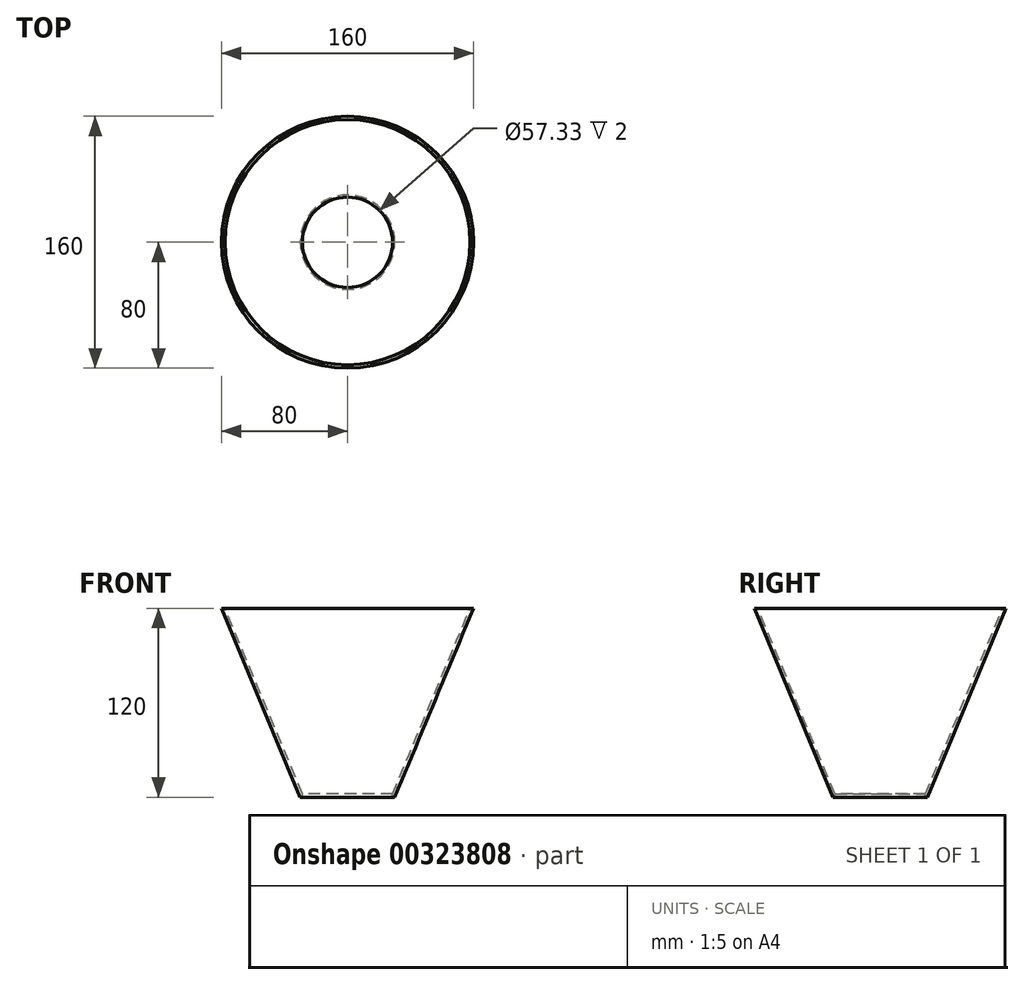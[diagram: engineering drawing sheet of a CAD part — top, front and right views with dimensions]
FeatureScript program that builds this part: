
annotation { "Feature Type Name" : "Feature", "Feature Type Description" : "" }
export const myFeature = defineFeature(function(context is Context, id is Id, definition is map)
    precondition{}
    {
        {
            var Q0;
            Q0=qCreatedBy(makeId("Front.planeOp"),FACE);
            var sketch = newSketch(context, id + "F0", { "sketchPlane" : qUnion([Q0])});
            skLineSegment(sketch, "E0", {"start": v(0, 0) * mm, "end": v(0, -120) * mm});
            skLineSegment(sketch, "E1", {"start": v(0, 0) * mm, "end": v(0, 240) * mm});
            skLineSegment(sketch, "E2", {"start": v(0, 240) * mm, "end": v(-180, 240) * mm});
            skLineSegment(sketch, "E3", {"start": v(0, -120) * mm, "end": v(-30, -120) * mm});
            skLineSegment(sketch, "E4", {"start": v(-180, 240) * mm, "end": v(-30, -120) * mm});
            skLineSegment(sketch, "E5", {"start": v(0, 0) * mm, "end": v(-80, 0) * mm});
            skSolve(sketch);
        }
        {
            var Q0;
            Q0=makeQuery(id+"F0.imprint","IMPRINT",FACE,{"disambiguationData":[TD([[makeQuery(id+"F0.imprint","IMPRINT",EDGE,{"derivedFrom":sQuery(id+"F0.wireOp",EDGE,"E0")}),-1.0]])]});
            var Q1;
            Q1=sQuery(id+"F0.wireOp",EDGE,"E0");
            revolve(context, id + "F1", {"entities" : qUnion([Q0]), "axis" : qUnion([Q1]), "revolveType" : RevolveType.FULL});
        }
        {
            var Q0;
            Q0=makeQuery(id+"F1.opRevolve","SWEPT_FACE",FACE,{"disambiguationData":[OSD([sQuery(id+"F0.wireOp",EDGE,"E5")])]});
            shell(context, id + "F2", {"entities" : qUnion([Q0]), "thickness" : 2 * mm});
        }
        {
            var Q0;
            Q0=makeQuery(id+"F2.opShell","OFFSET_FACE",FACE,{"disambiguationData":[OSD([sQuery(id+"F0.wireOp",EDGE,"E3")])]});
            extrude(context, id + "F3", {"entities" : qUnion([Q0]), "operationType" : NewBodyOperationType.REMOVE, "oppositeDirection" : true, "depth" : 25 * mm});
        }
    });
